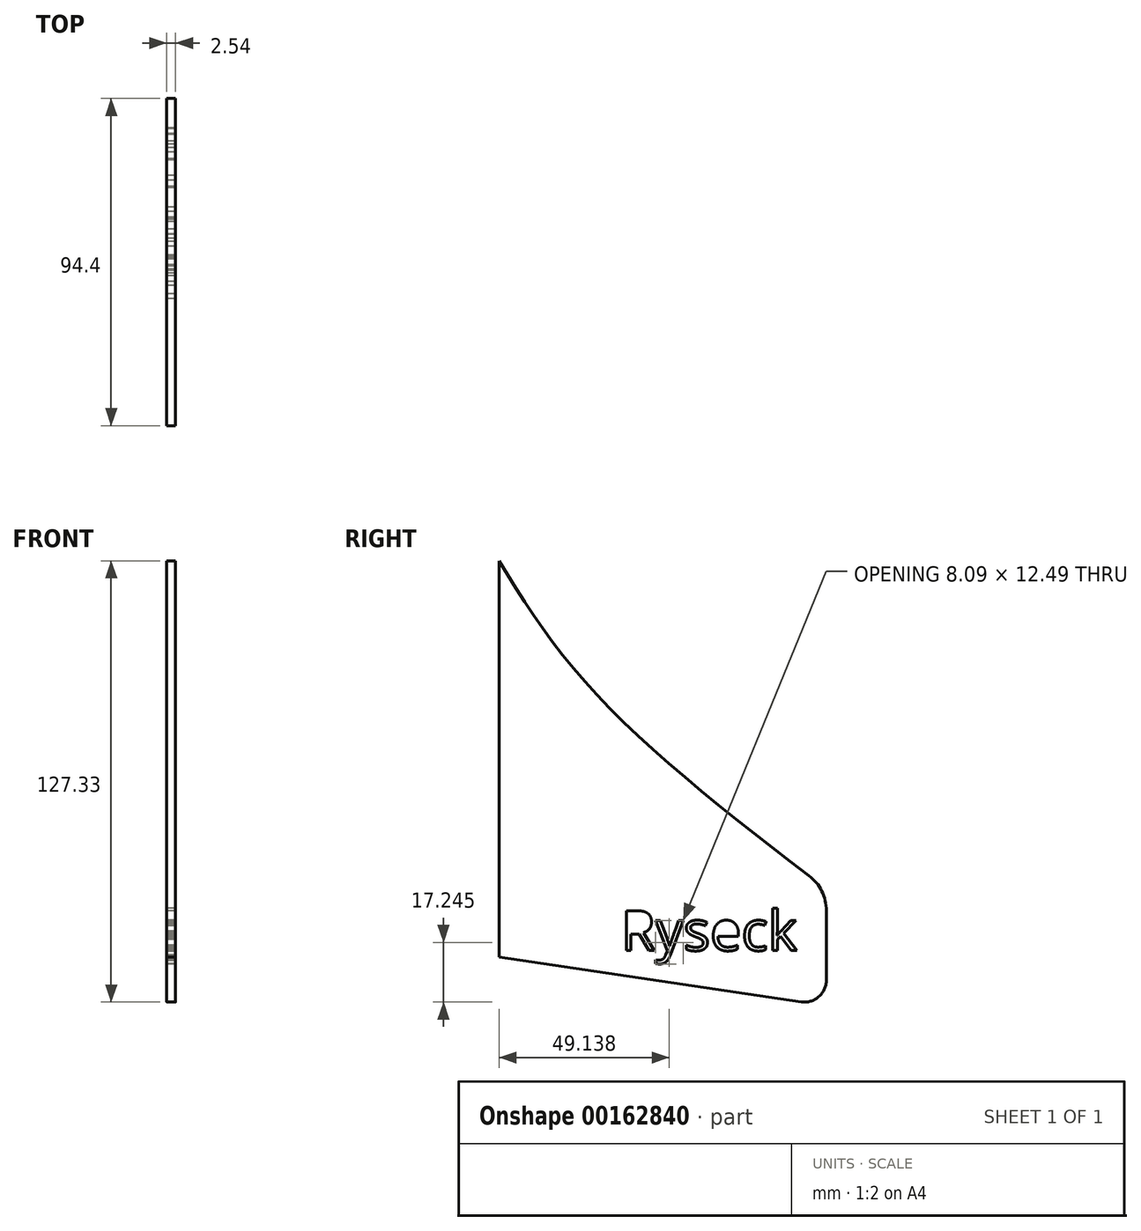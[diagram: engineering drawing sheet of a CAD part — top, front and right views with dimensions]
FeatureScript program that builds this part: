
annotation { "Feature Type Name" : "Feature", "Feature Type Description" : "" }
export const myFeature = defineFeature(function(context is Context, id is Id, definition is map)
    precondition{}
    {
        {
            var Q0;
            Q0=qCreatedBy(makeId("Right.planeOp"),FACE);
            var sketch = newSketch(context, id + "F0", { "sketchPlane" : qUnion([Q0])});
            skLineSegment(sketch, "E0.left", {"start": v(22.91, 54.36) * mm, "end": v(22.91, 44.3) * mm});
            skLineSegment(sketch, "E1", {"start": v(117.31, -46.58) * mm, "end": v(117.31, -66.62) * mm});
            skLineSegment(sketch, "E2", {"start": v(110.03, -72.9) * mm, "end": v(22.91, -59.94) * mm});
            skFitSpline(sketch, "E3", {"points": [v(22.91, 54.36) * mm, v(52.69, 14.06) * mm, v(117.31, -40.27) * mm], "startDerivative": vector(57.48, -95.9) * mm, "endDerivative": vector(128.43, -97) * mm});
            skArc(sketch, "E4.filletArc", {"start": v(117.31, -46.58) * mm, "mid": v(116, -40.94) * mm, "end": v(112.3, -36.47) * mm});
            skPoint(sketch, "E5.visualSharp", {"position": v(117.31, -73.99) * mm});
            skArc(sketch, "E5.filletArc", {"start": v(110.03, -72.9) * mm, "mid": v(115.11, -71.43) * mm, "end": v(117.31, -66.62) * mm});
            skText(sketch, "E6", { "text": "Ryseck", "fontName": "OpenSans-Regular.ttf"});
            skLineSegment(sketch, "E7.bottom", {"start": v(22.91, 44.3) * mm, "end": v(12.68, 44.3) * mm});
            skLineSegment(sketch, "E7.top", {"start": v(22.91, 37.04) * mm, "end": v(12.68, 37.04) * mm});
            skLineSegment(sketch, "E7.right", {"start": v(12.68, 44.3) * mm, "end": v(12.68, 37.04) * mm});
            skLineSegment(sketch, "E8.bottom", {"start": v(22.91, 18.07) * mm, "end": v(12.68, 18.07) * mm});
            skLineSegment(sketch, "E8.top", {"start": v(22.91, 11.52) * mm, "end": v(12.68, 11.52) * mm});
            skLineSegment(sketch, "E8.right", {"start": v(12.68, 18.07) * mm, "end": v(12.68, 11.52) * mm});
            skLineSegment(sketch, "E9.bottom", {"start": v(22.91, -32.5) * mm, "end": v(12.82, -32.5) * mm});
            skLineSegment(sketch, "E9.top", {"start": v(22.91, -38.36) * mm, "end": v(12.82, -38.36) * mm});
            skLineSegment(sketch, "E9.right", {"start": v(12.82, -32.5) * mm, "end": v(12.82, -38.36) * mm});
            skLineSegment(sketch, "E10.bottom", {"start": v(22.91, -50.54) * mm, "end": v(12.68, -50.54) * mm});
            skLineSegment(sketch, "E10.top", {"start": v(22.91, -57.56) * mm, "end": v(12.68, -57.56) * mm});
            skLineSegment(sketch, "E10.right", {"start": v(12.68, -50.54) * mm, "end": v(12.68, -57.56) * mm});
            skLineSegment(sketch, "E11.trimOffspring", {"start": v(22.91, -57.56) * mm, "end": v(22.91, -59.94) * mm});
            skLineSegment(sketch, "E12.trimOffspring", {"start": v(22.91, 11.52) * mm, "end": v(22.91, -32.5) * mm});
            skLineSegment(sketch, "E13.trimOffspring", {"start": v(22.91, 37.04) * mm, "end": v(22.91, 18.07) * mm});
            skLineSegment(sketch, "E14.trimOffspring", {"start": v(22.91, -38.36) * mm, "end": v(22.91, -50.54) * mm});
            skLineSegment(sketch, "E15", {"start": v(22.91, 44.3) * mm, "end": v(22.91, -57.56) * mm});
            const initialGuessF0  = {"E6": [0.05803, -0.0581, 1, 0, 0.0116]};
            skSetInitialGuess(sketch, initialGuessF0);
            skSolve(sketch);
        }
        {
            var Q0;
            Q0=makeQuery(id+"F0.imprint","IMPRINT",FACE,{"disambiguationData":[TD([[makeQuery(id+"F0.imprint","IMPRINT",EDGE,{"derivedFrom":sQuery(id+"F0.wireOp",EDGE,"E0.left")}),1.0]])]});
            extrude(context, id + "F1", {"entities" : qUnion([Q0]), "depth" : 2.54 * mm});
        }
    });
